# Revit family: 0047253
name_source: partatom
category: Lighting Fixtures
revit_build: Autodesk Revit 2017 (Build: 20160225_1515(x64)
units: mm (PartAtom-declared; Revit-internal decimal feet)

## family parameters
Cut with Voids When Loaded = No
Host = Face
Light Source = Yes
OmniClass Number = 23.80.70.00
OmniClass Title = Lighting
Part Type = Normal
Room Calculation Point = No
Round Connector Dimension = Use Diameter
Shared = No

## types (1)
- 0047253 Quadro UGR16 600x600 DALI 4450LM 830
    Apparent Load = 36 VA
    Assembly Code = D5020200
    ClassificationName = Uniclass2015
    ClassificationValue = EF_70_80
    Color Filter = 16777215
    Cost = 0 $
    Default Elevation = 1219 mm
    Dimming Lamp Color Temperature Shift = <None>
    DimmingControlOptions = DALI dimmable
    DocumentationLiterature = https://www.sylvania-lighting.com
    ElectricShockClassification = Class II
    Emit Shape Visible in Rendering = No
    Emit from Rectangle Length = 525 mm
    Emit from Rectangle Width = 525 mm
    IfcExportAs = IfcLightFixtureType
    IfcExportType = IfcLightFixtureType
    ImpactProtectionIndex = IK08
    IngressProtection = IP20
    InputNominalFrequency = 50/60 Hz
    InputVoltage = 220-240 V AC
    Keynote = 16500
    Lamp = LED
    LampColourTemperature = 3000 K
    LampNominalLuminous = 2024 lm
    LampsType = LED
    LuminaireType = panel
    LuminousEfficacy = 56.38 lm/W
    Manufacturer = Feilo Sylvania
    ManufacturerName = Feilo Sylvania
    Material_1_SYL = Body-Matrix-wh
    Material_2_SYL = <By Category>
    Material_3_SYL = <By Category>
    Material_4_SYL = <By Category>
    Model = Quadro UGR16 600x600 DALI 4450LM 830
    ModelNumber = 0047253
    ModelReference = Quadro UGR16 600x600 DALI 4450LM 830
    Name = Quadro UGR16 600x600 DALI 4450LM 830
    NominalDepth = 595 mm  [stored 1.9521 ft]
    NominalHeight = 10 mm  [stored 0.0328084 ft]
    NominalLength = 595 mm  [stored 1.9521 ft]
    Photometric Web File = 0047253.ies
    PowerConsumption = 35.9 W
    PowerFactor = 0
    Tilt Angle = -90.00°
    Type Image = <None>
    TypeName = Quadro UGR16 600x600 DALI 4450LM 830
    URL = http://www.sylvania-lighting.com
    Voltage = 230 V
    Width_SYL = 595 mm  [stored 1.9521 ft]

note: [stored X ft] marks values corroborated as IEEE doubles in the binary element streams (Revit-internal decimal feet)

## geometry (parser evidence)
native form markers: Sweep x5
no freeform markers — native parametric forms only
